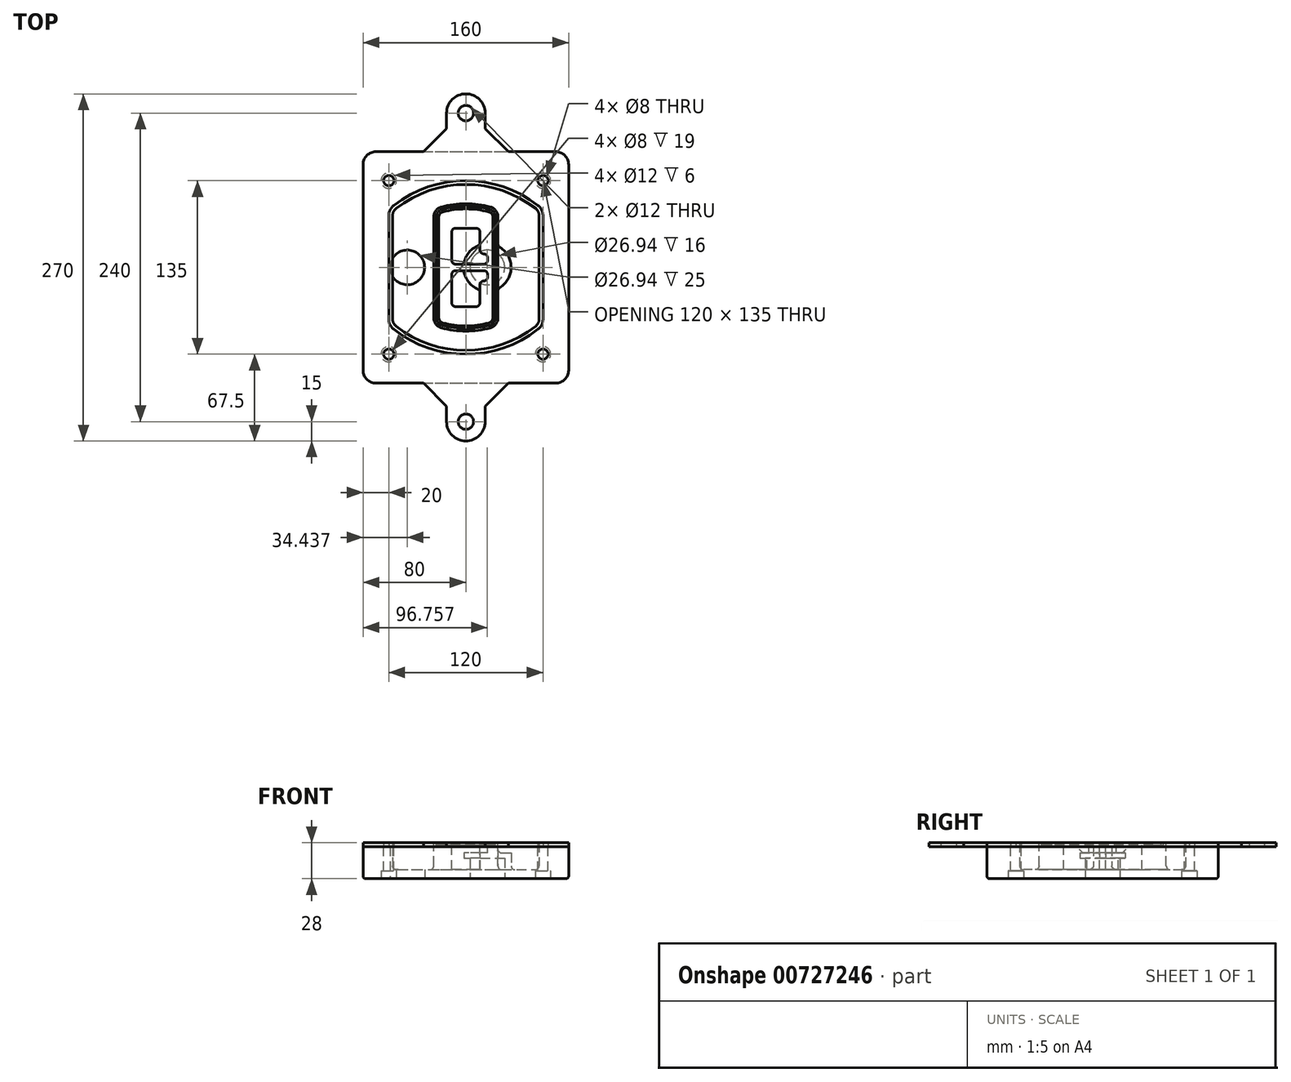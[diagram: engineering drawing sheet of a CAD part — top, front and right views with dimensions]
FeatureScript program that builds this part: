
annotation { "Feature Type Name" : "Feature", "Feature Type Description" : "" }
export const myFeature = defineFeature(function(context is Context, id is Id, definition is map)
    precondition{}
    {
        {
            var Q0;
            Q0=qCreatedBy(makeId("Top.planeOp"),FACE);
            var sketch = newSketch(context, id + "F0", { "sketchPlane" : qUnion([Q0])});
            skPoint(sketch, "E0.rect.middle", {"position": v(0, 0) * mm});
            skLineSegment(sketch, "E1.bottom", {"start": v(-70, -90) * mm, "end": v(70, -90) * mm});
            skLineSegment(sketch, "E1.top", {"start": v(-70, 90) * mm, "end": v(70, 90) * mm});
            skLineSegment(sketch, "E1.left", {"start": v(-80, -80) * mm, "end": v(-80, 80) * mm});
            skLineSegment(sketch, "E1.right", {"start": v(80, -80) * mm, "end": v(80, 80) * mm});
            skLineSegment(sketch, "E2", {"start": v(-80, 90) * mm, "end": v(80, -90) * mm, "construction": true});
            skLineSegment(sketch, "E3", {"start": v(80, 90) * mm, "end": v(-80, -90) * mm, "construction": true});
            skCircle(sketch, "E4", {"center": v(-60, 67.5) * mm, "radius": 4 * mm});
            skCircle(sketch, "E5", {"center": v(60, 67.5) * mm, "radius": 4 * mm});
            skCircle(sketch, "E6", {"center": v(60, -67.5) * mm, "radius": 4 * mm});
            skCircle(sketch, "E7", {"center": v(-60, -67.5) * mm, "radius": 4 * mm});
            skLineSegment(sketch, "E8", {"start": v(-60, 67.5) * mm, "end": v(60, 67.5) * mm, "construction": true});
            skLineSegment(sketch, "E9", {"start": v(60, 67.5) * mm, "end": v(60, -67.5) * mm, "construction": true});
            skLineSegment(sketch, "E10", {"start": v(60, -67.5) * mm, "end": v(-60, -67.5) * mm, "construction": true});
            skLineSegment(sketch, "E11", {"start": v(-60, -67.5) * mm, "end": v(-60, 67.5) * mm, "construction": true});
            skLineSegment(sketch, "E12", {"start": v(-60, 40.3) * mm, "end": v(-60, -40.3) * mm});
            skLineSegment(sketch, "E13", {"start": v(60, 40.3) * mm, "end": v(60, -40.3) * mm});
            skArc(sketch, "E14", {"start": v(56.15, 48.18) * mm, "mid": v(0, 67.5) * mm, "end": v(-56.15, 48.18) * mm});
            skArc(sketch, "E15", {"start": v(-56.15, -48.18) * mm, "mid": v(0, -67.5) * mm, "end": v(56.15, -48.18) * mm});
            skLineSegment(sketch, "E16", {"start": v(-60, 0) * mm, "end": v(60, 0) * mm, "construction": true});
            skPoint(sketch, "E17.visualSharp", {"position": v(-60, -45) * mm});
            skArc(sketch, "E17.filletArc", {"start": v(-60, -40.3) * mm, "mid": v(-58.99, -44.68) * mm, "end": v(-56.15, -48.18) * mm});
            skPoint(sketch, "E18.visualSharp", {"position": v(-60, 45) * mm});
            skArc(sketch, "E18.filletArc", {"start": v(-56.15, 48.18) * mm, "mid": v(-58.99, 44.68) * mm, "end": v(-60, 40.3) * mm});
            skPoint(sketch, "E19.visualSharp", {"position": v(60, 45) * mm});
            skArc(sketch, "E19.filletArc", {"start": v(60, 40.3) * mm, "mid": v(58.99, 44.68) * mm, "end": v(56.15, 48.18) * mm});
            skPoint(sketch, "E20.visualSharp", {"position": v(60, -45) * mm});
            skArc(sketch, "E20.filletArc", {"start": v(56.15, -48.18) * mm, "mid": v(58.99, -44.68) * mm, "end": v(60, -40.3) * mm});
            skPoint(sketch, "E21.visualSharp", {"position": v(-80, 90) * mm});
            skArc(sketch, "E21.filletArc", {"start": v(-70, 90) * mm, "mid": v(-77.07, 87.07) * mm, "end": v(-80, 80) * mm});
            skPoint(sketch, "E22.visualSharp", {"position": v(80, 90) * mm});
            skArc(sketch, "E22.filletArc", {"start": v(80, 80) * mm, "mid": v(77.07, 87.07) * mm, "end": v(70, 90) * mm});
            skPoint(sketch, "E23.visualSharp", {"position": v(80, -90) * mm});
            skArc(sketch, "E23.filletArc", {"start": v(70, -90) * mm, "mid": v(77.07, -87.07) * mm, "end": v(80, -80) * mm});
            skPoint(sketch, "E24.visualSharp", {"position": v(-80, -90) * mm});
            skArc(sketch, "E24.filletArc", {"start": v(-80, -80) * mm, "mid": v(-77.07, -87.07) * mm, "end": v(-70, -90) * mm});
            skArc(sketch, "E25.0", {"start": v(57, 40.3) * mm, "mid": v(56.3, 43.36) * mm, "end": v(54.3, 45.81) * mm});
            skLineSegment(sketch, "E25.1", {"start": v(57, 40.3) * mm, "end": v(57, -40.3) * mm});
            skArc(sketch, "E25.2", {"start": v(54.3, -45.81) * mm, "mid": v(56.3, -43.36) * mm, "end": v(57, -40.3) * mm});
            skArc(sketch, "E25.3", {"start": v(-54.3, -45.81) * mm, "mid": v(0, -64.5) * mm, "end": v(54.3, -45.81) * mm});
            skArc(sketch, "E25.4", {"start": v(-57, -40.3) * mm, "mid": v(-56.3, -43.36) * mm, "end": v(-54.3, -45.81) * mm});
            skArc(sketch, "E25.5", {"start": v(54.3, 45.81) * mm, "mid": v(0, 64.5) * mm, "end": v(-54.3, 45.81) * mm});
            skLineSegment(sketch, "E25.6", {"start": v(-57, 40.3) * mm, "end": v(-57, -40.3) * mm});
            skArc(sketch, "E25.7", {"start": v(-54.3, 45.81) * mm, "mid": v(-56.3, 43.36) * mm, "end": v(-57, 40.3) * mm});
            skArc(sketch, "E26.0", {"start": v(-58.62, 51.33) * mm, "mid": v(-62.58, 46.43) * mm, "end": v(-64, 40.3) * mm});
            skArc(sketch, "E26.1", {"start": v(58.62, 51.33) * mm, "mid": v(0, 71.5) * mm, "end": v(-58.62, 51.33) * mm});
            skArc(sketch, "E26.2", {"start": v(64, 40.3) * mm, "mid": v(62.58, 46.43) * mm, "end": v(58.62, 51.33) * mm});
            skLineSegment(sketch, "E26.3", {"start": v(64, 40.3) * mm, "end": v(64, -40.3) * mm});
            skArc(sketch, "E26.4", {"start": v(58.62, -51.33) * mm, "mid": v(62.58, -46.43) * mm, "end": v(64, -40.3) * mm});
            skLineSegment(sketch, "E26.5", {"start": v(-64, 40.3) * mm, "end": v(-64, -40.3) * mm});
            skArc(sketch, "E26.6", {"start": v(-58.62, -51.33) * mm, "mid": v(0, -71.5) * mm, "end": v(58.62, -51.33) * mm});
            skArc(sketch, "E26.7", {"start": v(-64, -40.3) * mm, "mid": v(-62.58, -46.43) * mm, "end": v(-58.62, -51.33) * mm});
            skSolve(sketch);
        }
        {
            var Q0;
            Q0=makeQuery(id+"F0.imprint","IMPRINT",FACE,{"disambiguationData":[TD([[makeQuery(id+"F0.imprint","IMPRINT",EDGE,{"derivedFrom":sQuery(id+"F0.wireOp",EDGE,"E1.bottom")}),1.0]])]});
            var Q1;
            Q1=makeQuery(id+"F0.imprint","IMPRINT",FACE,{"disambiguationData":[TD([[makeQuery(id+"F0.imprint","IMPRINT",EDGE,{"derivedFrom":sQuery(id+"F0.wireOp",EDGE,"E12")}),1.0]])]});
            var Q2;
            Q2=makeQuery(id+"F0.imprint","IMPRINT",FACE,{"disambiguationData":[TD([[makeQuery(id+"F0.imprint","IMPRINT",EDGE,{"derivedFrom":sQuery(id+"F0.wireOp",EDGE,"E25.0")}),1.0]])]});
            var Q3;
            Q3=makeQuery(id+"F0.imprint","IMPRINT",FACE,{"disambiguationData":[TD([[makeQuery(id+"F0.imprint","IMPRINT",EDGE,{"derivedFrom":sQuery(id+"F0.wireOp",EDGE,"E12")}),-1.0]])]});
            extrude(context, id + "F1", {"entities" : qUnion([Q0, Q1, Q2, Q3]), "oppositeDirection" : true, "depth" : 25 * mm});
        }
        {
            var Q0;
            Q0=makeQuery(id+"F0.imprint","IMPRINT",FACE,{"disambiguationData":[TD([[makeQuery(id+"F0.imprint","IMPRINT",EDGE,{"derivedFrom":sQuery(id+"F0.wireOp",EDGE,"E12")}),1.0]])]});
            extrude(context, id + "F2", {"entities" : qUnion([Q0]), "operationType" : NewBodyOperationType.ADD, "depth" : 3 * mm});
        }
        {
            var Q0;
            Q0=makeQuery(id+"F0.imprint","IMPRINT",FACE,{"disambiguationData":[TD([[makeQuery(id+"F0.imprint","IMPRINT",EDGE,{"derivedFrom":sQuery(id+"F0.wireOp",EDGE,"E25.0")}),1.0]])]});
            extrude(context, id + "F3", {"entities" : qUnion([Q0]), "operationType" : NewBodyOperationType.REMOVE, "oppositeDirection" : true, "depth" : 18 * mm});
        }
        {
            var Q0;
            Q0=makeQuery(id+"F2.opExtrude","CAP_FACE",FACE,{"disambiguationData":[OSD([sQuery(id+"F0.wireOp",EDGE,"E12"),sQuery(id+"F0.wireOp",EDGE,"E13"),sQuery(id+"F0.wireOp",EDGE,"E14"),sQuery(id+"F0.wireOp",EDGE,"E15"),sQuery(id+"F0.wireOp",EDGE,"E17.filletArc"),sQuery(id+"F0.wireOp",EDGE,"E18.filletArc"),sQuery(id+"F0.wireOp",EDGE,"E19.filletArc"),sQuery(id+"F0.wireOp",EDGE,"E20.filletArc"),sQuery(id+"F0.wireOp",EDGE,"E25.0"),sQuery(id+"F0.wireOp",EDGE,"E25.1"),sQuery(id+"F0.wireOp",EDGE,"E25.2"),sQuery(id+"F0.wireOp",EDGE,"E25.3"),sQuery(id+"F0.wireOp",EDGE,"E25.4"),sQuery(id+"F0.wireOp",EDGE,"E25.5"),sQuery(id+"F0.wireOp",EDGE,"E25.6"),sQuery(id+"F0.wireOp",EDGE,"E25.7")])],"isStart":false});
            var sketch = newSketch(context, id + "F4", { "sketchPlane" : qUnion([Q0])});
            skArc(sketch, "E27.0", {"start": v(-19.08, -46.97) * mm, "mid": v(0, -49.5) * mm, "end": v(19.08, -46.97) * mm});
            skArc(sketch, "E28.0", {"start": v(19.08, 46.97) * mm, "mid": v(0, 49.5) * mm, "end": v(-19.08, 46.97) * mm});
            skLineSegment(sketch, "E29", {"start": v(-25, 39.25) * mm, "end": v(-25, -39.25) * mm});
            skLineSegment(sketch, "E30", {"start": v(25, 39.25) * mm, "end": v(25, -39.25) * mm});
            skLineSegment(sketch, "E31", {"start": v(-25, 45.1) * mm, "end": v(25, 45.1) * mm, "construction": true});
            skLineSegment(sketch, "E32", {"start": v(-25, -45.1) * mm, "end": v(25, -45.1) * mm, "construction": true});
            skPoint(sketch, "E33.visualSharp", {"position": v(-25, 45.1) * mm});
            skArc(sketch, "E33.filletArc", {"start": v(-19.08, 46.97) * mm, "mid": v(-23.35, 44.11) * mm, "end": v(-25, 39.25) * mm});
            skPoint(sketch, "E34.visualSharp", {"position": v(25, 45.1) * mm});
            skArc(sketch, "E34.filletArc", {"start": v(25, 39.25) * mm, "mid": v(23.35, 44.11) * mm, "end": v(19.08, 46.97) * mm});
            skPoint(sketch, "E35.visualSharp", {"position": v(25, -45.1) * mm});
            skArc(sketch, "E35.filletArc", {"start": v(19.08, -46.97) * mm, "mid": v(23.35, -44.11) * mm, "end": v(25, -39.25) * mm});
            skPoint(sketch, "E36.visualSharp", {"position": v(-25, -45.1) * mm});
            skArc(sketch, "E36.filletArc", {"start": v(-25, -39.25) * mm, "mid": v(-23.35, -44.11) * mm, "end": v(-19.08, -46.97) * mm});
            skArc(sketch, "E37.0", {"start": v(54.3, 45.81) * mm, "mid": v(0, 64.5) * mm, "end": v(-54.3, 45.81) * mm});
            skArc(sketch, "E37.1", {"start": v(-54.3, 45.81) * mm, "mid": v(-56.3, 43.36) * mm, "end": v(-57, 40.3) * mm});
            skLineSegment(sketch, "E37.2", {"start": v(-57, 40.3) * mm, "end": v(-57, -40.3) * mm});
            skArc(sketch, "E37.3", {"start": v(-57, -40.3) * mm, "mid": v(-56.3, -43.36) * mm, "end": v(-54.3, -45.81) * mm});
            skArc(sketch, "E37.4", {"start": v(-54.3, -45.81) * mm, "mid": v(0, -64.5) * mm, "end": v(54.3, -45.81) * mm});
            skArc(sketch, "E37.5", {"start": v(54.3, -45.81) * mm, "mid": v(56.3, -43.36) * mm, "end": v(57, -40.3) * mm});
            skLineSegment(sketch, "E37.6", {"start": v(57, 40.3) * mm, "end": v(57, -40.3) * mm});
            skArc(sketch, "E37.7", {"start": v(57, 40.3) * mm, "mid": v(56.3, 43.36) * mm, "end": v(54.3, 45.81) * mm});
            skLineSegment(sketch, "E38.0", {"start": v(23, 39.25) * mm, "end": v(23, -39.25) * mm});
            skArc(sketch, "E38.1", {"start": v(18.56, -45.04) * mm, "mid": v(21.76, -42.9) * mm, "end": v(23, -39.25) * mm});
            skArc(sketch, "E38.2", {"start": v(-18.56, -45.04) * mm, "mid": v(0, -47.5) * mm, "end": v(18.56, -45.04) * mm});
            skArc(sketch, "E38.3", {"start": v(-23, -39.25) * mm, "mid": v(-21.76, -42.9) * mm, "end": v(-18.56, -45.04) * mm});
            skLineSegment(sketch, "E38.4", {"start": v(-23, 39.25) * mm, "end": v(-23, -39.25) * mm});
            skArc(sketch, "E38.5", {"start": v(23, 39.25) * mm, "mid": v(21.76, 42.9) * mm, "end": v(18.56, 45.04) * mm});
            skArc(sketch, "E38.6", {"start": v(-18.56, 45.04) * mm, "mid": v(-21.76, 42.9) * mm, "end": v(-23, 39.25) * mm});
            skArc(sketch, "E38.7", {"start": v(18.56, 45.04) * mm, "mid": v(0, 47.5) * mm, "end": v(-18.56, 45.04) * mm});
            skArc(sketch, "E39.0", {"start": v(21, 39.25) * mm, "mid": v(20.18, 41.68) * mm, "end": v(18.04, 43.1) * mm});
            skLineSegment(sketch, "E39.1", {"start": v(21, 39.25) * mm, "end": v(21, -39.25) * mm});
            skArc(sketch, "E39.2", {"start": v(18.04, -43.1) * mm, "mid": v(20.18, -41.68) * mm, "end": v(21, -39.25) * mm});
            skArc(sketch, "E39.3", {"start": v(-18.04, -43.1) * mm, "mid": v(0, -45.5) * mm, "end": v(18.04, -43.1) * mm});
            skArc(sketch, "E39.4", {"start": v(-21, -39.25) * mm, "mid": v(-20.18, -41.68) * mm, "end": v(-18.04, -43.1) * mm});
            skArc(sketch, "E39.5", {"start": v(18.04, 43.1) * mm, "mid": v(0, 45.5) * mm, "end": v(-18.04, 43.1) * mm});
            skLineSegment(sketch, "E39.6", {"start": v(-21, 39.25) * mm, "end": v(-21, -39.25) * mm});
            skArc(sketch, "E39.7", {"start": v(-18.04, 43.1) * mm, "mid": v(-20.18, 41.68) * mm, "end": v(-21, 39.25) * mm});
            skLineSegment(sketch, "E40", {"start": v(-25, 0) * mm, "end": v(25, 0) * mm, "construction": true});
            skLineSegment(sketch, "E41", {"start": v(-11, 5.5) * mm, "end": v(-11, 27.5) * mm});
            skLineSegment(sketch, "E42", {"start": v(-8, 30.5) * mm, "end": v(8, 30.5) * mm});
            skLineSegment(sketch, "E43", {"start": v(11, 27.5) * mm, "end": v(11, 13.5) * mm});
            skLineSegment(sketch, "E44", {"start": v(14, 10.5) * mm, "end": v(14, 10.5) * mm});
            skLineSegment(sketch, "E45", {"start": v(17, 7.5) * mm, "end": v(17, 5.5) * mm});
            skLineSegment(sketch, "E46", {"start": v(14, 2.5) * mm, "end": v(-8, 2.5) * mm});
            skPoint(sketch, "E47.visualSharp", {"position": v(-11, 30.5) * mm});
            skArc(sketch, "E47.filletArc", {"start": v(-8, 30.5) * mm, "mid": v(-10.12, 29.62) * mm, "end": v(-11, 27.5) * mm});
            skPoint(sketch, "E48.visualSharp", {"position": v(11, 30.5) * mm});
            skArc(sketch, "E48.filletArc", {"start": v(11, 27.5) * mm, "mid": v(10.12, 29.62) * mm, "end": v(8, 30.5) * mm});
            skPoint(sketch, "E49.visualSharp", {"position": v(11, 10.5) * mm});
            skArc(sketch, "E49.filletArc", {"start": v(11, 13.5) * mm, "mid": v(11.88, 11.38) * mm, "end": v(14, 10.5) * mm});
            skPoint(sketch, "E50.visualSharp", {"position": v(17, 10.5) * mm});
            skArc(sketch, "E50.filletArc", {"start": v(17, 7.5) * mm, "mid": v(16.12, 9.62) * mm, "end": v(14, 10.5) * mm});
            skPoint(sketch, "E51.visualSharp", {"position": v(17, 2.5) * mm});
            skArc(sketch, "E51.filletArc", {"start": v(14, 2.5) * mm, "mid": v(16.12, 3.38) * mm, "end": v(17, 5.5) * mm});
            skPoint(sketch, "E52.visualSharp", {"position": v(-11, 2.5) * mm});
            skArc(sketch, "E52.filletArc", {"start": v(-11, 5.5) * mm, "mid": v(-10.12, 3.38) * mm, "end": v(-8, 2.5) * mm});
            skLineSegment(sketch, "E53.0.MirrorCS", {"start": v(14, -2.5) * mm, "end": v(-8, -2.5) * mm});
            skArc(sketch, "E54.0.MirrorCS", {"start": v(-11, -5.5) * mm, "mid": v(-10.12, -3.38) * mm, "end": v(-8, -2.5) * mm});
            skLineSegment(sketch, "E55.0.MirrorCS", {"start": v(-11, -5.5) * mm, "end": v(-11, -27.5) * mm});
            skArc(sketch, "E56.0.MirrorCS", {"start": v(-8, -30.5) * mm, "mid": v(-10.12, -29.62) * mm, "end": v(-11, -27.5) * mm});
            skLineSegment(sketch, "E57.0.MirrorCS", {"start": v(-8, -30.5) * mm, "end": v(8, -30.5) * mm});
            skArc(sketch, "E58.0.MirrorCS", {"start": v(11, -27.5) * mm, "mid": v(10.12, -29.62) * mm, "end": v(8, -30.5) * mm});
            skLineSegment(sketch, "E59.0.MirrorCS", {"start": v(11, -27.5) * mm, "end": v(11, -13.5) * mm});
            skArc(sketch, "E60.0.MirrorCS", {"start": v(11, -13.5) * mm, "mid": v(11.88, -11.38) * mm, "end": v(14, -10.5) * mm});
            skArc(sketch, "E61.0.MirrorCS", {"start": v(17, -7.5) * mm, "mid": v(16.12, -9.62) * mm, "end": v(14, -10.5) * mm});
            skLineSegment(sketch, "E62.0.MirrorCS", {"start": v(17, -7.5) * mm, "end": v(17, -5.5) * mm});
            skArc(sketch, "E63.0.MirrorCS", {"start": v(14, -2.5) * mm, "mid": v(16.12, -3.38) * mm, "end": v(17, -5.5) * mm});
            skSolve(sketch);
        }
        {
            var Q0;
            Q0=makeQuery(id+"F4.imprint","IMPRINT",FACE,{"disambiguationData":[TD([[makeQuery(id+"F4.imprint","IMPRINT",EDGE,{"derivedFrom":sQuery(id+"F4.wireOp",EDGE,"E27.0")}),1.0]])]});
            var Q1;
            Q1=makeQuery(id+"F4.imprint","IMPRINT",FACE,{"disambiguationData":[TD([[makeQuery(id+"F4.imprint","IMPRINT",EDGE,{"derivedFrom":sQuery(id+"F4.wireOp",EDGE,"E38.0")}),-1.0]])]});
            var Q2;
            Q2=makeQuery(id+"F4.imprint","IMPRINT",FACE,{"disambiguationData":[TD([[makeQuery(id+"F4.imprint","IMPRINT",EDGE,{"derivedFrom":sQuery(id+"F4.wireOp",EDGE,"E39.0")}),1.0]])]});
            extrude(context, id + "F5", {"entities" : qUnion([Q0, Q1, Q2]), "operationType" : NewBodyOperationType.ADD, "endBound" : BoundingType.UP_TO_NEXT, "oppositeDirection" : true, "depth" : 25 * mm});
        }
        {
            var Q0;
            Q0=makeQuery(id+"F4.imprint","IMPRINT",FACE,{"disambiguationData":[TD([[makeQuery(id+"F4.imprint","IMPRINT",EDGE,{"derivedFrom":sQuery(id+"F4.wireOp",EDGE,"E38.0")}),-1.0]])]});
            extrude(context, id + "F6", {"entities" : qUnion([Q0]), "operationType" : NewBodyOperationType.REMOVE, "oppositeDirection" : true, "depth" : 2 * mm});
        }
        {
            var Q0;
            Q0=makeQuery(id+"F1.opExtrude","CAP_FACE",FACE,{"disambiguationData":[OSD([sQuery(id+"F0.wireOp",EDGE,"E1.bottom"),sQuery(id+"F0.wireOp",EDGE,"E1.top"),sQuery(id+"F0.wireOp",EDGE,"E1.left"),sQuery(id+"F0.wireOp",EDGE,"E1.right"),sQuery(id+"F0.wireOp",EDGE,"E4"),sQuery(id+"F0.wireOp",EDGE,"E5"),sQuery(id+"F0.wireOp",EDGE,"E6"),sQuery(id+"F0.wireOp",EDGE,"E7"),sQuery(id+"F0.wireOp",EDGE,"E21.filletArc"),sQuery(id+"F0.wireOp",EDGE,"E22.filletArc"),sQuery(id+"F0.wireOp",EDGE,"E23.filletArc"),sQuery(id+"F0.wireOp",EDGE,"E24.filletArc")])],"isStart":false});
            var sketch = newSketch(context, id + "F7", { "sketchPlane" : qUnion([Q0])});
            skCircle(sketch, "E64", {"center": v(16.76, 0) * mm, "radius": 13.47 * mm});
            skCircle(sketch, "E65", {"center": v(-45.56, 0) * mm, "radius": 13.47 * mm});
            skLineSegment(sketch, "E66", {"start": v(80, 0) * mm, "end": v(-80, 0) * mm});
            skCircle(sketch, "E67", {"center": v(16.76, 0) * mm, "radius": 18.47 * mm});
            skCircle(sketch, "E68", {"center": v(60, -67.5) * mm, "radius": 6 * mm});
            skCircle(sketch, "E69", {"center": v(-60, -67.5) * mm, "radius": 6 * mm});
            skCircle(sketch, "E70", {"center": v(-60, 67.5) * mm, "radius": 6 * mm});
            skCircle(sketch, "E71", {"center": v(60, 67.5) * mm, "radius": 6 * mm});
            skSolve(sketch);
        }
        {
            var Q0;
            {var subQ1=sQuery(id+"F7.wireOp",EDGE,"E66");var subQ4=sQuery(id+"F7.wireOp",EDGE,"E64");var subQ6=makeQuery(id+"F7.imprint","INTERSECT",VERTEX,{"disambiguationData":[OD(0.0)],"derivedFrom":[subQ4,subQ1]});Q0=makeQuery(id+"F7.imprint","IMPRINT",FACE,{"disambiguationData":[TD([[makeQuery(id+"F7.imprint","IMPRINT",EDGE,{"disambiguationData":[TD([[subQ6,-1.0]])],"derivedFrom":subQ4}),-1.0]])]});}
            var Q1;
            {var subQ0=sQuery(id+"F7.wireOp",EDGE,"E66");var subQ1=sQuery(id+"F7.wireOp",EDGE,"E64");var subQ3=makeQuery(id+"F7.imprint","INTERSECT",VERTEX,{"disambiguationData":[OD(0.0)],"derivedFrom":[subQ1,subQ0]});Q1=makeQuery(id+"F7.imprint","IMPRINT",FACE,{"disambiguationData":[TD([[makeQuery(id+"F7.imprint","IMPRINT",EDGE,{"disambiguationData":[TD([[subQ3,-1.0]])],"derivedFrom":subQ1}),1.0]])]});}
            var Q2;
            {var subQ0=sQuery(id+"F7.wireOp",EDGE,"E66");var subQ1=sQuery(id+"F7.wireOp",EDGE,"E64");var subQ3=makeQuery(id+"F7.imprint","INTERSECT",VERTEX,{"disambiguationData":[OD(0.0)],"derivedFrom":[subQ1,subQ0]});Q2=makeQuery(id+"F7.imprint","IMPRINT",FACE,{"disambiguationData":[TD([[makeQuery(id+"F7.imprint","IMPRINT",EDGE,{"disambiguationData":[TD([[subQ3,1.0]])],"derivedFrom":subQ1}),1.0]])]});}
            var Q3;
            {var subQ1=sQuery(id+"F7.wireOp",EDGE,"E66");var subQ4=sQuery(id+"F7.wireOp",EDGE,"E64");var subQ6=makeQuery(id+"F7.imprint","INTERSECT",VERTEX,{"disambiguationData":[OD(0.0)],"derivedFrom":[subQ4,subQ1]});Q3=makeQuery(id+"F7.imprint","IMPRINT",FACE,{"disambiguationData":[TD([[makeQuery(id+"F7.imprint","IMPRINT",EDGE,{"disambiguationData":[TD([[subQ6,1.0]])],"derivedFrom":subQ4}),-1.0]])]});}
            extrude(context, id + "F8", {"entities" : qUnion([Q0, Q1, Q2, Q3]), "operationType" : NewBodyOperationType.ADD, "oppositeDirection" : true, "depth" : 20 * mm});
        }
        {
            var Q0;
            {var subQ0=sQuery(id+"F7.wireOp",EDGE,"E66");var subQ1=sQuery(id+"F7.wireOp",EDGE,"E64");var subQ3=makeQuery(id+"F7.imprint","INTERSECT",VERTEX,{"disambiguationData":[OD(0.0)],"derivedFrom":[subQ1,subQ0]});Q0=makeQuery(id+"F7.imprint","IMPRINT",FACE,{"disambiguationData":[TD([[makeQuery(id+"F7.imprint","IMPRINT",EDGE,{"disambiguationData":[TD([[subQ3,-1.0]])],"derivedFrom":subQ1}),1.0]])]});}
            var Q1;
            {var subQ0=sQuery(id+"F7.wireOp",EDGE,"E66");var subQ1=sQuery(id+"F7.wireOp",EDGE,"E64");var subQ3=makeQuery(id+"F7.imprint","INTERSECT",VERTEX,{"disambiguationData":[OD(0.0)],"derivedFrom":[subQ1,subQ0]});Q1=makeQuery(id+"F7.imprint","IMPRINT",FACE,{"disambiguationData":[TD([[makeQuery(id+"F7.imprint","IMPRINT",EDGE,{"disambiguationData":[TD([[subQ3,1.0]])],"derivedFrom":subQ1}),1.0]])]});}
            extrude(context, id + "F9", {"entities" : qUnion([Q0, Q1]), "operationType" : NewBodyOperationType.REMOVE, "oppositeDirection" : true, "depth" : 16 * mm});
        }
        {
            var Q0;
            {var subQ0=sQuery(id+"F7.wireOp",EDGE,"E66");var subQ1=sQuery(id+"F7.wireOp",EDGE,"E65");var subQ3=makeQuery(id+"F7.imprint","INTERSECT",VERTEX,{"disambiguationData":[OD(0.0)],"derivedFrom":[subQ1,subQ0]});Q0=makeQuery(id+"F7.imprint","IMPRINT",FACE,{"disambiguationData":[TD([[makeQuery(id+"F7.imprint","IMPRINT",EDGE,{"disambiguationData":[TD([[subQ3,-1.0]])],"derivedFrom":subQ1}),1.0]])]});}
            var Q1;
            {var subQ0=sQuery(id+"F7.wireOp",EDGE,"E66");var subQ1=sQuery(id+"F7.wireOp",EDGE,"E65");var subQ3=makeQuery(id+"F7.imprint","INTERSECT",VERTEX,{"disambiguationData":[OD(0.0)],"derivedFrom":[subQ1,subQ0]});Q1=makeQuery(id+"F7.imprint","IMPRINT",FACE,{"disambiguationData":[TD([[makeQuery(id+"F7.imprint","IMPRINT",EDGE,{"disambiguationData":[TD([[subQ3,1.0]])],"derivedFrom":subQ1}),1.0]])]});}
            extrude(context, id + "F10", {"entities" : qUnion([Q0, Q1]), "operationType" : NewBodyOperationType.REMOVE, "oppositeDirection" : true, "depth" : 25 * mm});
        }
        {
            var Q0;
            Q0=makeQuery(id+"F7.imprint","IMPRINT",FACE,{"disambiguationData":[TD([[makeQuery(id+"F7.imprint","IMPRINT",EDGE,{"derivedFrom":sQuery(id+"F7.wireOp",EDGE,"E68")}),1.0]])]});
            var Q1;
            Q1=makeQuery(id+"F7.imprint","IMPRINT",FACE,{"disambiguationData":[TD([[makeQuery(id+"F7.imprint","IMPRINT",EDGE,{"derivedFrom":makeQuery(id+"F1.opExtrude","CAP_EDGE",EDGE,{"disambiguationData":[OSD([sQuery(id+"F0.wireOp",EDGE,"E5")])],"isStart":false})}),-1.0]])]});
            var Q2;
            Q2=makeQuery(id+"F7.imprint","IMPRINT",FACE,{"disambiguationData":[TD([[makeQuery(id+"F7.imprint","IMPRINT",EDGE,{"derivedFrom":sQuery(id+"F7.wireOp",EDGE,"E69")}),1.0]])]});
            var Q3;
            Q3=makeQuery(id+"F7.imprint","IMPRINT",FACE,{"disambiguationData":[TD([[makeQuery(id+"F7.imprint","IMPRINT",EDGE,{"derivedFrom":makeQuery(id+"F1.opExtrude","CAP_EDGE",EDGE,{"disambiguationData":[OSD([sQuery(id+"F0.wireOp",EDGE,"E4")])],"isStart":false})}),-1.0]])]});
            var Q4;
            Q4=makeQuery(id+"F7.imprint","IMPRINT",FACE,{"disambiguationData":[TD([[makeQuery(id+"F7.imprint","IMPRINT",EDGE,{"derivedFrom":sQuery(id+"F7.wireOp",EDGE,"E70")}),1.0]])]});
            var Q5;
            Q5=makeQuery(id+"F7.imprint","IMPRINT",FACE,{"disambiguationData":[TD([[makeQuery(id+"F7.imprint","IMPRINT",EDGE,{"derivedFrom":makeQuery(id+"F1.opExtrude","CAP_EDGE",EDGE,{"disambiguationData":[OSD([sQuery(id+"F0.wireOp",EDGE,"E7")])],"isStart":false})}),-1.0]])]});
            var Q6;
            Q6=makeQuery(id+"F7.imprint","IMPRINT",FACE,{"disambiguationData":[TD([[makeQuery(id+"F7.imprint","IMPRINT",EDGE,{"derivedFrom":sQuery(id+"F7.wireOp",EDGE,"E71")}),1.0]])]});
            var Q7;
            Q7=makeQuery(id+"F7.imprint","IMPRINT",FACE,{"disambiguationData":[TD([[makeQuery(id+"F7.imprint","IMPRINT",EDGE,{"derivedFrom":makeQuery(id+"F1.opExtrude","CAP_EDGE",EDGE,{"disambiguationData":[OSD([sQuery(id+"F0.wireOp",EDGE,"E6")])],"isStart":false})}),-1.0]])]});
            extrude(context, id + "F11", {"entities" : qUnion([Q0, Q1, Q2, Q3, Q4, Q5, Q6, Q7]), "operationType" : NewBodyOperationType.REMOVE, "oppositeDirection" : true, "depth" : 6 * mm});
        }
        {
            var Q0;
            Q0=makeQuery(id+"F9.boolean.opBoolean","COPY",FACE,{"derivedFrom":makeQuery(id+"F9.opExtrude","CAP_FACE",FACE,{"disambiguationData":[OSD([sQuery(id+"F7.wireOp",EDGE,"E64")])],"isStart":false})});
            var sketch = newSketch(context, id + "F12", { "sketchPlane" : qUnion([Q0])});
            skArc(sketch, "E72.0", {"start": v(11, 17.55) * mm, "mid": v(2.57, 11.82) * mm, "end": v(-1.54, 2.5) * mm});
            skArc(sketch, "E72.1", {"start": v(-1.54, -2.5) * mm, "mid": v(2.57, -11.82) * mm, "end": v(11, -17.55) * mm});
            skLineSegment(sketch, "E73", {"start": v(-1.54, -2.5) * mm, "end": v(14, -2.5) * mm});
            skLineSegment(sketch, "E74.0", {"start": v(14, 2.5) * mm, "end": v(-1.54, 2.5) * mm});
            skArc(sketch, "E74.1", {"start": v(14, 2.5) * mm, "mid": v(16.12, 3.38) * mm, "end": v(17, 5.5) * mm});
            skLineSegment(sketch, "E74.2", {"start": v(17, 7.5) * mm, "end": v(17, 5.5) * mm});
            skArc(sketch, "E74.3", {"start": v(17, 7.5) * mm, "mid": v(16.12, 9.62) * mm, "end": v(14, 10.5) * mm});
            skArc(sketch, "E74.4", {"start": v(11, 13.5) * mm, "mid": v(11.88, 11.38) * mm, "end": v(14, 10.5) * mm});
            skLineSegment(sketch, "E74.5", {"start": v(11, 17.55) * mm, "end": v(11, 13.5) * mm});
            skLineSegment(sketch, "E74.7", {"start": v(14, -2.5) * mm, "end": v(-1.54, -2.5) * mm});
            skArc(sketch, "E74.8", {"start": v(14, -2.5) * mm, "mid": v(16.12, -3.38) * mm, "end": v(17, -5.5) * mm});
            skLineSegment(sketch, "E74.9", {"start": v(17, -7.5) * mm, "end": v(17, -5.5) * mm});
            skArc(sketch, "E74.10", {"start": v(17, -7.5) * mm, "mid": v(16.12, -9.62) * mm, "end": v(14, -10.5) * mm});
            skArc(sketch, "E74.11", {"start": v(11, -13.5) * mm, "mid": v(11.88, -11.38) * mm, "end": v(14, -10.5) * mm});
            skLineSegment(sketch, "E74.12", {"start": v(11, -17.55) * mm, "end": v(11, -13.5) * mm});
            skPoint(sketch, "E75.orphan", {"position": v(11, -27.5) * mm});
            skPoint(sketch, "E76.orphan", {"position": v(-8, -2.5) * mm});
            skPoint(sketch, "E77.orphan", {"position": v(-8, 2.5) * mm});
            skPoint(sketch, "E78.orphan", {"position": v(11, 27.5) * mm});
            skSolve(sketch);
        }
        {
            var Q0;
            {var subQ7=sQuery(id+"F12.wireOp",EDGE,"E72.0");var subQ14=sQuery(id+"F12.wireOp",EDGE,"E72.1");var subQ16=sQuery(id+"F12.wireOp",EDGE,"E74.1");var subQ18=sQuery(id+"F12.wireOp",EDGE,"E74.8");Q0=qUnion([makeQuery(id+"F12.imprint","IMPRINT",FACE,{"disambiguationData":[TD([[makeQuery(id+"F12.imprint","IMPRINT",EDGE,{"derivedFrom":subQ7}),1.0]])]}),makeQuery(id+"F12.imprint","IMPRINT",FACE,{"disambiguationData":[TD([[makeQuery(id+"F12.imprint","IMPRINT",EDGE,{"derivedFrom":subQ14}),1.0]])]}),makeQuery(id+"F12.imprint","IMPRINT",FACE,{"disambiguationData":[TD([[makeQuery(id+"F12.imprint","IMPRINT",EDGE,{"derivedFrom":subQ16}),1.0]])]}),makeQuery(id+"F12.imprint","IMPRINT",FACE,{"disambiguationData":[TD([[makeQuery(id+"F12.imprint","IMPRINT",EDGE,{"derivedFrom":subQ18}),-1.0]])]})]);}
            var Q1;
            Q1=makeQuery(id+"F5.boolean.opBoolean","SPLIT",FACE,{"disambiguationData":[TD([makeQuery(id+"F5.opExtrude","SWEPT_FACE",FACE,{"disambiguationData":[OSD([sQuery(id+"F4.wireOp",EDGE,"E41")])]})])],"derivedFrom":makeQuery(id+"F3.boolean.opBoolean","COPY",FACE,{"derivedFrom":makeQuery(id+"F3.opExtrude","CAP_FACE",FACE,{"disambiguationData":[OSD([sQuery(id+"F0.wireOp",EDGE,"E25.0"),sQuery(id+"F0.wireOp",EDGE,"E25.1"),sQuery(id+"F0.wireOp",EDGE,"E25.2"),sQuery(id+"F0.wireOp",EDGE,"E25.3"),sQuery(id+"F0.wireOp",EDGE,"E25.4"),sQuery(id+"F0.wireOp",EDGE,"E25.5"),sQuery(id+"F0.wireOp",EDGE,"E25.6"),sQuery(id+"F0.wireOp",EDGE,"E25.7")])],"isStart":false})})});
            extrude(context, id + "F13", {"entities" : qUnion([Q0]), "operationType" : NewBodyOperationType.REMOVE, "endBound" : BoundingType.UP_TO_SURFACE, "endBoundEntityFace" : qUnion([Q1]), "depth" : 25 * mm});
        }
        {
            var Q0;
            Q0=makeQuery(id+"F3.boolean.opBoolean","COPY",EDGE,{"derivedFrom":makeQuery(id+"F3.opExtrude","CAP_EDGE",EDGE,{"disambiguationData":[OSD([sQuery(id+"F0.wireOp",EDGE,"E25.6")])],"isStart":false})});
            var Q1;
            Q1=makeQuery(id+"F8.boolean.opBoolean","INTERSECT",EDGE,{"derivedFrom":[makeQuery(id+"F5.opExtrude","SWEPT_FACE",FACE,{"disambiguationData":[OSD([sQuery(id+"F4.wireOp",EDGE,"E30")])]}),makeQuery(id+"F8.opExtrude","CAP_FACE",FACE,{"disambiguationData":[OSD([sQuery(id+"F7.wireOp",EDGE,"E67")])],"isStart":false})]});
            var Q2;
            Q2=makeQuery(id+"F8.boolean.opBoolean","INTERSECT",EDGE,{"disambiguationData":[OD(1.0)],"derivedFrom":[makeQuery(id+"F5.opExtrude","SWEPT_FACE",FACE,{"disambiguationData":[OSD([sQuery(id+"F4.wireOp",EDGE,"E30")])]}),makeQuery(id+"F8.opExtrude","SWEPT_FACE",FACE,{"disambiguationData":[OSD([sQuery(id+"F7.wireOp",EDGE,"E67")])]})]});
            var Q3;
            {var subQ0=sQuery(id+"F4.wireOp",EDGE,"E30");Q3=makeQuery(id+"F8.boolean.opBoolean","SPLIT",EDGE,{"disambiguationData":[TD([makeQuery(id+"F5.opExtrude","SWEPT_FACE",FACE,{"disambiguationData":[OSD([sQuery(id+"F4.wireOp",EDGE,"E35.filletArc")])]})])],"derivedFrom":makeQuery(id+"F5.opExtrude","CAP_EDGE",EDGE,{"disambiguationData":[OSD([subQ0])],"isStart":false})});}
            var Q4;
            {var subQ0=sQuery(id+"F0.wireOp",EDGE,"E25.7");var subQ1=sQuery(id+"F0.wireOp",EDGE,"E25.1");var subQ2=sQuery(id+"F0.wireOp",EDGE,"E25.6");var subQ3=sQuery(id+"F0.wireOp",EDGE,"E25.5");var subQ4=sQuery(id+"F0.wireOp",EDGE,"E25.4");var subQ5=sQuery(id+"F0.wireOp",EDGE,"E25.0");var subQ6=sQuery(id+"F0.wireOp",EDGE,"E25.2");var subQ7=sQuery(id+"F0.wireOp",EDGE,"E25.3");Q4=makeQuery(id+"F8.boolean.opBoolean","INTERSECT",EDGE,{"derivedFrom":[makeQuery(id+"F5.boolean.opBoolean","SPLIT",FACE,{"disambiguationData":[TD([makeQuery(id+"F2.opExtrude","SWEPT_FACE",FACE,{"disambiguationData":[OSD([subQ5])]})])],"derivedFrom":makeQuery(id+"F3.boolean.opBoolean","COPY",FACE,{"derivedFrom":makeQuery(id+"F3.opExtrude","CAP_FACE",FACE,{"disambiguationData":[OSD([subQ5,subQ1,subQ6,subQ7,subQ4,subQ3,subQ2,subQ0])],"isStart":false})})}),makeQuery(id+"F8.opExtrude","SWEPT_FACE",FACE,{"disambiguationData":[OSD([sQuery(id+"F7.wireOp",EDGE,"E67")])]})]});}
            var Q5;
            Q5=makeQuery(id+"F8.boolean.opBoolean","INTERSECT",EDGE,{"disambiguationData":[OD(0.0)],"derivedFrom":[makeQuery(id+"F5.opExtrude","SWEPT_FACE",FACE,{"disambiguationData":[OSD([sQuery(id+"F4.wireOp",EDGE,"E30")])]}),makeQuery(id+"F8.opExtrude","SWEPT_FACE",FACE,{"disambiguationData":[OSD([sQuery(id+"F7.wireOp",EDGE,"E67")])]})]});
            fillet(context, id + "F14", {"entities" : qUnion([Q0, Q1, Q2, Q3, Q4, Q5]), "radius" : 3 * mm, "tangentPropagation" : true, "allowEdgeOverflow" : false});
        }
        {
            var Q0;
            Q0=makeQuery(id+"F1.opExtrude","CAP_EDGE",EDGE,{"disambiguationData":[OSD([sQuery(id+"F0.wireOp",EDGE,"E1.bottom")])],"isStart":false});
            fillet(context, id + "F15", {"entities" : qUnion([Q0]), "radius" : 2 * mm, "tangentPropagation" : true, "allowEdgeOverflow" : false});
        }
        {
            var Q0;
            {var subQ0=sQuery(id+"F0.wireOp",EDGE,"E21.filletArc");var subQ1=sQuery(id+"F0.wireOp",EDGE,"E7");var subQ2=sQuery(id+"F0.wireOp",EDGE,"E6");var subQ3=sQuery(id+"F0.wireOp",EDGE,"E5");var subQ4=sQuery(id+"F0.wireOp",EDGE,"E4");var subQ5=sQuery(id+"F0.wireOp",EDGE,"E22.filletArc");var subQ6=sQuery(id+"F0.wireOp",EDGE,"E1.bottom");var subQ7=sQuery(id+"F0.wireOp",EDGE,"E1.right");var subQ8=sQuery(id+"F0.wireOp",EDGE,"E1.top");var subQ9=sQuery(id+"F0.wireOp",EDGE,"E1.left");var subQ10=sQuery(id+"F0.wireOp",EDGE,"E23.filletArc");var subQ11=sQuery(id+"F0.wireOp",EDGE,"E24.filletArc");Q0=makeQuery(id+"F2.boolean.opBoolean","SPLIT",FACE,{"disambiguationData":[TD([makeQuery(id+"F1.opExtrude","SWEPT_FACE",FACE,{"disambiguationData":[OSD([subQ6])]})])],"derivedFrom":makeQuery(id+"F1.opExtrude","CAP_FACE",FACE,{"disambiguationData":[OSD([subQ6,subQ8,subQ9,subQ7,subQ4,subQ3,subQ2,subQ1,subQ0,subQ5,subQ10,subQ11])],"isStart":true})});}
            var sketch = newSketch(context, id + "F16", { "sketchPlane" : qUnion([Q0])});
            skSolve(sketch);
        }
        {
            var Q0;
            Q0=makeQuery(id+"F16.imprint","IMPRINT",FACE,{"disambiguationData":[TD([[makeQuery(id+"F16.imprint","IMPRINT",EDGE,{"derivedFrom":makeQuery(id+"F1.opExtrude","CAP_EDGE",EDGE,{"disambiguationData":[OSD([sQuery(id+"F0.wireOp",EDGE,"E1.bottom")])],"isStart":true})}),1.0]])]});
            var sketch = newSketch(context, id + "F17", { "sketchPlane" : qUnion([Q0])});
            skLineSegment(sketch, "E79", {"start": v(-33, 90) * mm, "end": v(-15, 108) * mm});
            skLineSegment(sketch, "E80", {"start": v(-15, 108) * mm, "end": v(-15, 120) * mm});
            skLineSegment(sketch, "E81", {"start": v(33, 90) * mm, "end": v(15, 108) * mm});
            skLineSegment(sketch, "E82", {"start": v(15, 108) * mm, "end": v(15, 120) * mm});
            skCircle(sketch, "E83", {"center": v(0, 120) * mm, "radius": 6 * mm});
            skLineSegment(sketch, "E84", {"start": v(0, 120) * mm, "end": v(0, 90) * mm, "construction": true});
            skArc(sketch, "E85", {"start": v(15, 120) * mm, "mid": v(0, 135) * mm, "end": v(-15, 120) * mm});
            skLineSegment(sketch, "E86", {"start": v(80, 0) * mm, "end": v(-80, 0) * mm, "construction": true});
            skLineSegment(sketch, "E87.MirrorCS", {"start": v(15, -108) * mm, "end": v(15, -120) * mm});
            skLineSegment(sketch, "E88.MirrorCS", {"start": v(33, -90) * mm, "end": v(15, -108) * mm});
            skLineSegment(sketch, "E89.MirrorCS", {"start": v(0, -120) * mm, "end": v(0, -90) * mm});
            skLineSegment(sketch, "E90.MirrorCS", {"start": v(-15, -108) * mm, "end": v(-15, -120) * mm});
            skArc(sketch, "E91.MirrorCS", {"start": v(15, -120) * mm, "mid": v(0, -135) * mm, "end": v(-15, -120) * mm});
            skCircle(sketch, "E92.MirrorC", {"center": v(0, -120) * mm, "radius": 6 * mm});
            skLineSegment(sketch, "E93.MirrorCS", {"start": v(-33, -90) * mm, "end": v(-15, -108) * mm});
            skLineSegment(sketch, "E94", {"start": v(-33, 90) * mm, "end": v(33, 90) * mm});
            skLineSegment(sketch, "E95", {"start": v(-33, -90) * mm, "end": v(33, -90) * mm});
            skLineSegment(sketch, "E96", {"start": v(0, -90) * mm, "end": v(0, 90) * mm, "construction": true});
            skSolve(sketch);
        }
        {
            var Q0;
            Q0 = qSketchRegion(id + "F17", true);
            var Q1;
            {var subQ8=sQuery(id+"F17.wireOp",EDGE,"E94");Q1=makeQuery(id+"F17.imprint","IMPRINT",FACE,{"disambiguationData":[TD([[makeQuery(id+"F17.imprint","IMPRINT",EDGE,{"derivedFrom":subQ8}),-1.0]])]});}
            var Q2;
            Q2=makeQuery(id+"F2.opExtrude","CAP_FACE",FACE,{"disambiguationData":[OSD([sQuery(id+"F0.wireOp",EDGE,"E12"),sQuery(id+"F0.wireOp",EDGE,"E13"),sQuery(id+"F0.wireOp",EDGE,"E14"),sQuery(id+"F0.wireOp",EDGE,"E15"),sQuery(id+"F0.wireOp",EDGE,"E17.filletArc"),sQuery(id+"F0.wireOp",EDGE,"E18.filletArc"),sQuery(id+"F0.wireOp",EDGE,"E19.filletArc"),sQuery(id+"F0.wireOp",EDGE,"E20.filletArc"),sQuery(id+"F0.wireOp",EDGE,"E25.0"),sQuery(id+"F0.wireOp",EDGE,"E25.1"),sQuery(id+"F0.wireOp",EDGE,"E25.2"),sQuery(id+"F0.wireOp",EDGE,"E25.3"),sQuery(id+"F0.wireOp",EDGE,"E25.4"),sQuery(id+"F0.wireOp",EDGE,"E25.5"),sQuery(id+"F0.wireOp",EDGE,"E25.6"),sQuery(id+"F0.wireOp",EDGE,"E25.7")])],"isStart":false});
            extrude(context, id + "F18", {"entities" : qUnion([Q0, Q1]), "endBound" : BoundingType.UP_TO_SURFACE, "depth" : 25 * mm, "endBoundEntityFace" : qUnion([Q2]), "offsetDistance" : 25 * mm});
        }
    });
